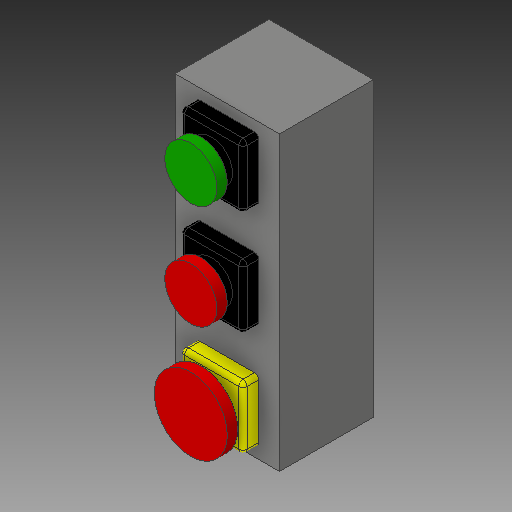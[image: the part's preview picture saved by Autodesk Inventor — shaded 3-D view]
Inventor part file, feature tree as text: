
AUTODESK INVENTOR PART (.ipt)
format: ipt  version: 2019 (Build 230136000, 136)  size: 232,448 bytes
history: native  units: mm
features: extrude x4, sketch x4, fillet x2
ambient origin geometry x8: Origin, YZ Plane, XZ Plane, XY Plane, X Axis, Y Axis, Z Axis, Center Point
bodies: Solid1 (feature_tree)
feature tree (10):
  extrude  "Extrusion1"  Depth=100.0mm
  extrude  "Extrusion2"  Depth=20.0mm
  fillet  "Fillet1"  Radius=80.0mm
  fillet  "Fillet2"  Radius=270.0mm
  extrude  "Extrusion3"  Depth=10.0mm
  extrude  "Extrusion4"  Depth=110.0mm
  sketch  "Sketch1"  dims[d0=280.0mm d1=100.0mm]
  sketch  "Sketch2"  dims[d2=90.0mm d3=0.0mm d4=20.0mm d5=80.0mm d6=270.0mm]
  sketch  "Sketch3"  dims[d7=210.0mm d8=10.0mm]
  sketch  "Sketch4"  dims[d9=70.0mm d10=110.0mm d11=170.0mm d12=15.0mm d13=0.0mm d14=4.0mm d15=4.0mm d16=240.0mm d17=40.0mm d18=50.0mm d19=30.0mm d21=100.0mm d22=10.0mm d24=10.0mm d26=10.0mm d27=0.0mm d28=50.0mm d29=20.0mm d31=100.0mm d32=10.0mm d34=10.0mm d36=200.0mm d37=70.0mm d38=10.0mm d39=0.0mm]
